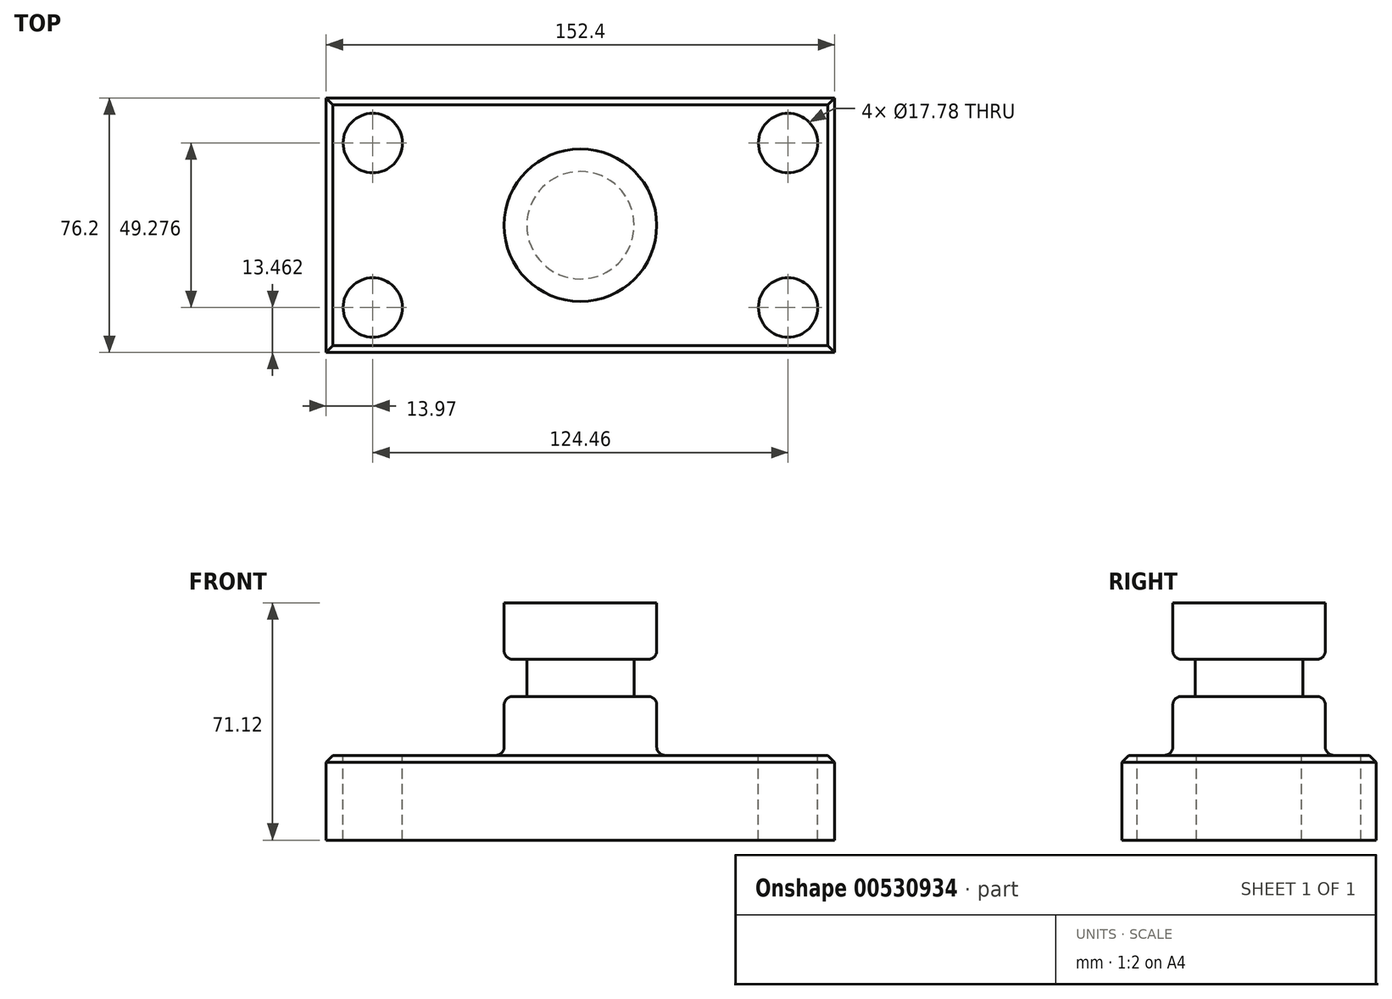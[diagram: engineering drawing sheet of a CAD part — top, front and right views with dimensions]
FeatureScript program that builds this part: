
annotation { "Feature Type Name" : "Feature", "Feature Type Description" : "" }
export const myFeature = defineFeature(function(context is Context, id is Id, definition is map)
    precondition{}
    {
        {
            var Q0;
            Q0=qCreatedBy(makeId("Top.planeOp"),FACE);
            var sketch = newSketch(context, id + "F0", { "sketchPlane" : qUnion([Q0])});
            skLineSegment(sketch, "E0.bottom", {"start": v(76.2, 38.1) * mm, "end": v(-76.2, 38.1) * mm});
            skLineSegment(sketch, "E0.top", {"start": v(76.2, -38.1) * mm, "end": v(-76.2, -38.1) * mm});
            skLineSegment(sketch, "E0.left", {"start": v(76.2, 38.1) * mm, "end": v(76.2, -38.1) * mm});
            skLineSegment(sketch, "E0.right", {"start": v(-76.2, 38.1) * mm, "end": v(-76.2, -38.1) * mm});
            skPoint(sketch, "E0.middle", {"position": v(0, 0) * mm});
            skSolve(sketch);
        }
        {
            var Q0;
            Q0=makeQuery(id+"F0.imprint","IMPRINT",FACE,{"disambiguationData":[TD([[makeQuery(id+"F0.imprint","IMPRINT",EDGE,{"derivedFrom":sQuery(id+"F0.wireOp",EDGE,"E0.bottom")}),1.0]])]});
            extrude(context, id + "F1", {"entities" : qUnion([Q0]), "depth" : 25.4 * mm, "offsetDistance" : 25.4 * mm});
        }
        {
            var Q0;
            Q0=makeQuery(id+"F1.opExtrude","CAP_FACE",FACE,{"disambiguationData":[OSD([sQuery(id+"F0.wireOp",EDGE,"E0.bottom"),sQuery(id+"F0.wireOp",EDGE,"E0.top"),sQuery(id+"F0.wireOp",EDGE,"E0.left"),sQuery(id+"F0.wireOp",EDGE,"E0.right")])],"isStart":false});
            var sketch = newSketch(context, id + "F2", { "sketchPlane" : qUnion([Q0])});
            skCircle(sketch, "E1", {"center": v(-62.23, 24.64) * mm, "radius": 8.9 * mm});
            skCircle(sketch, "E2", {"center": v(62.23, -24.64) * mm, "radius": 8.9 * mm});
            skCircle(sketch, "E3", {"center": v(62.23, 24.64) * mm, "radius": 8.9 * mm});
            skCircle(sketch, "E4", {"center": v(-62.23, -24.64) * mm, "radius": 8.9 * mm});
            skSolve(sketch);
        }
        {
            var Q0;
            Q0 = qSketchRegion(id + "F2", true);
            extrude(context, id + "F3", {"entities" : qUnion([Q0]), "operationType" : NewBodyOperationType.REMOVE, "oppositeDirection" : true, "depth" : 25.4 * mm, "offsetDistance" : 25.4 * mm});
        }
        {
            var Q0;
            Q0=makeQuery(id+"F1.opExtrude","CAP_EDGE",EDGE,{"disambiguationData":[OSD([sQuery(id+"F0.wireOp",EDGE,"E0.left")])],"isStart":false});
            var Q1;
            Q1=makeQuery(id+"F1.opExtrude","CAP_EDGE",EDGE,{"disambiguationData":[OSD([sQuery(id+"F0.wireOp",EDGE,"E0.bottom")])],"isStart":false});
            var Q2;
            Q2=makeQuery(id+"F1.opExtrude","CAP_EDGE",EDGE,{"disambiguationData":[OSD([sQuery(id+"F0.wireOp",EDGE,"E0.top")])],"isStart":false});
            var Q3;
            Q3=makeQuery(id+"F1.opExtrude","CAP_EDGE",EDGE,{"disambiguationData":[OSD([sQuery(id+"F0.wireOp",EDGE,"E0.right")])],"isStart":false});
            chamfer(context, id + "F4", {"entities" : qUnion([Q0, Q1, Q2, Q3]), "width" : 2.03 * mm, "tangentPropagation" : true});
        }
        {
            var Q0;
            Q0=qCreatedBy(makeId("Front.planeOp"),FACE);
            var sketch = newSketch(context, id + "F5", { "sketchPlane" : qUnion([Q0])});
            skLineSegment(sketch, "E5.bottom", {"start": v(0, 25.4) * mm, "end": v(22.86, 25.4) * mm});
            skLineSegment(sketch, "E5.top", {"start": v(0, 71.12) * mm, "end": v(22.86, 71.12) * mm});
            skLineSegment(sketch, "E5.left", {"start": v(0, 25.4) * mm, "end": v(0, 71.12) * mm});
            skLineSegment(sketch, "E5.right", {"start": v(22.86, 25.4) * mm, "end": v(22.86, 71.12) * mm});
            skSolve(sketch);
        }
        {
            var Q0;
            Q0=makeQuery(id+"F5.imprint","IMPRINT",FACE,{"disambiguationData":[TD([[makeQuery(id+"F5.imprint","IMPRINT",EDGE,{"derivedFrom":sQuery(id+"F5.wireOp",EDGE,"E5.bottom")}),1.0]])]});
            var Q1;
            Q1=sQuery(id+"F5.wireOp",EDGE,"E5.left");
            revolve(context, id + "F6", {"operationType" : NewBodyOperationType.ADD, "entities" : qUnion([Q0]), "axis" : qUnion([Q1]), "revolveType" : RevolveType.FULL});
        }
        {
            var Q0;
            Q0=qCreatedBy(makeId("Front.planeOp"),FACE);
            var sketch = newSketch(context, id + "F7", { "sketchPlane" : qUnion([Q0])});
            skLineSegment(sketch, "E6.bottom", {"start": v(16.1, 43.04) * mm, "end": v(23.01, 43.04) * mm});
            skLineSegment(sketch, "E6.top", {"start": v(16.1, 54.19) * mm, "end": v(23.01, 54.19) * mm});
            skLineSegment(sketch, "E6.left", {"start": v(16.1, 43.04) * mm, "end": v(16.1, 54.19) * mm});
            skLineSegment(sketch, "E6.right", {"start": v(23.01, 43.04) * mm, "end": v(23.01, 54.19) * mm});
            skSolve(sketch);
        }
        {
            var Q0;
            Q0=makeQuery(id+"F7.imprint","IMPRINT",FACE,{"disambiguationData":[TD([[makeQuery(id+"F7.imprint","IMPRINT",EDGE,{"derivedFrom":sQuery(id+"F7.wireOp",EDGE,"E6.bottom")}),1.0]])]});
            var Q1;
            Q1=makeQuery(id+"F6.opRevolve","SWEPT_FACE",FACE,{"disambiguationData":[OSD([sQuery(id+"F5.wireOp",EDGE,"E5.right")])]});
            revolve(context, id + "F8", {"operationType" : NewBodyOperationType.REMOVE, "entities" : qUnion([Q0]), "axis" : qUnion([Q1]), "revolveType" : RevolveType.FULL, "oppositeDirection" : true});
        }
        {
            var Q0;
            Q0=makeQuery(id+"F8.boolean.opBoolean","SPLIT",FACE,{"disambiguationData":[TD([makeQuery(id+"F8.opRevolve","SWEPT_FACE",FACE,{"disambiguationData":[OSD([sQuery(id+"F7.wireOp",EDGE,"E6.bottom")])]})])],"derivedFrom":makeQuery(id+"F6.opRevolve","SWEPT_FACE",FACE,{"disambiguationData":[OSD([sQuery(id+"F5.wireOp",EDGE,"E5.right")])]})});
            fillet(context, id + "F9", {"entities" : qUnion([Q0]), "radius" : 2.54 * mm, "tangentPropagation" : true, "allowEdgeOverflow" : false});
        }
        {
            var Q0;
            Q0=makeQuery(id+"F8.boolean.opBoolean","INTERSECT",EDGE,{"derivedFrom":[makeQuery(id+"F6.opRevolve","SWEPT_FACE",FACE,{"disambiguationData":[OSD([sQuery(id+"F5.wireOp",EDGE,"E5.right")])]}),makeQuery(id+"F8.opRevolve","SWEPT_FACE",FACE,{"disambiguationData":[OSD([sQuery(id+"F7.wireOp",EDGE,"E6.top")])]})]});
            fillet(context, id + "F10", {"entities" : qUnion([Q0]), "radius" : 2.54 * mm, "tangentPropagation" : true, "allowEdgeOverflow" : false});
        }
    });
